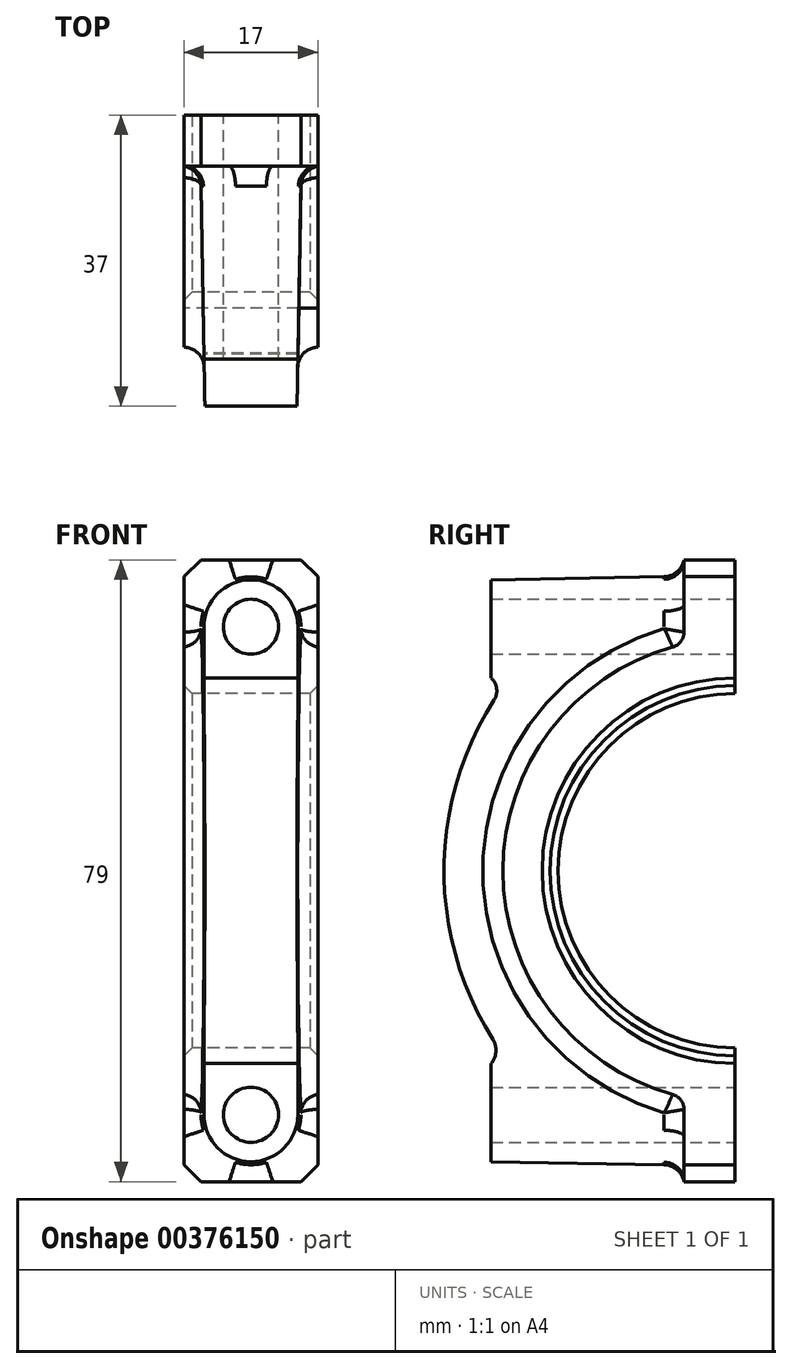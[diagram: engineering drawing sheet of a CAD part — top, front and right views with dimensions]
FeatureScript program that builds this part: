
annotation { "Feature Type Name" : "Feature", "Feature Type Description" : "" }
export const myFeature = defineFeature(function(context is Context, id is Id, definition is map)
    precondition{}
    {
        {
            var Q0;
            Q0=qCreatedBy(makeId("Top.planeOp"),FACE);
            var sketch = newSketch(context, id + "F0", { "sketchPlane" : qUnion([Q0])});
            skCircle(sketch, "E0", {"center": v(0, 31) * mm, "radius": 3.5 * mm});
            skCircle(sketch, "E1", {"center": v(0, 31) * mm, "radius": 6.5 * mm});
            skLineSegment(sketch, "E2", {"start": v(-13.97, 0) * mm, "end": v(15.82, 0) * mm, "construction": true});
            skLineSegment(sketch, "E3", {"start": v(-6.5, 31) * mm, "end": v(-6.5, 0) * mm});
            skLineSegment(sketch, "E4", {"start": v(-6.5, 0) * mm, "end": v(6.5, 0) * mm});
            skLineSegment(sketch, "E5", {"start": v(6.5, 0) * mm, "end": v(6.5, 31) * mm});
            skLineSegment(sketch, "E6", {"start": v(-6.35, 39.5) * mm, "end": v(6.35, 39.5) * mm});
            skLineSegment(sketch, "E7", {"start": v(6.35, 39.5) * mm, "end": v(8.5, 37.35) * mm});
            skLineSegment(sketch, "E8", {"start": v(8.5, 37.35) * mm, "end": v(8.5, 0) * mm});
            skLineSegment(sketch, "E9", {"start": v(8.5, 0) * mm, "end": v(-8.5, 0) * mm});
            skLineSegment(sketch, "E10", {"start": v(-8.5, 0) * mm, "end": v(-8.5, 37.35) * mm});
            skLineSegment(sketch, "E11", {"start": v(-8.5, 37.35) * mm, "end": v(-6.35, 39.5) * mm});
            skLineSegment(sketch, "E12", {"start": v(-6.5, 0) * mm, "end": v(-6.5, -31) * mm});
            skLineSegment(sketch, "E13", {"start": v(6.5, 0) * mm, "end": v(6.5, -31) * mm});
            skCircle(sketch, "E14", {"center": v(0, -31) * mm, "radius": 6.5 * mm});
            skCircle(sketch, "E15", {"center": v(0, -31) * mm, "radius": 3.5 * mm});
            skLineSegment(sketch, "E16", {"start": v(-8.5, 0) * mm, "end": v(-8.5, -37.35) * mm});
            skLineSegment(sketch, "E17", {"start": v(-8.5, -37.35) * mm, "end": v(-6.35, -39.5) * mm});
            skLineSegment(sketch, "E18", {"start": v(-6.35, -39.5) * mm, "end": v(6.35, -39.5) * mm});
            skLineSegment(sketch, "E19", {"start": v(6.35, -39.5) * mm, "end": v(8.5, -37.35) * mm});
            skLineSegment(sketch, "E20", {"start": v(8.5, -37.35) * mm, "end": v(8.5, 0) * mm});
            skSolve(sketch);
        }
        {
            var Q0;
            {var subQ1=sQuery(id+"F0.wireOp",EDGE,"E3");Q0=makeQuery(id+"F0.imprint","IMPRINT",FACE,{"disambiguationData":[TD([[makeQuery(id+"F0.imprint","IMPRINT",EDGE,{"derivedFrom":subQ1}),-1.0]])]});}
            var Q1;
            {var subQ0=sQuery(id+"F0.wireOp",EDGE,"E3");Q1=makeQuery(id+"F0.imprint","IMPRINT",FACE,{"disambiguationData":[TD([[makeQuery(id+"F0.imprint","IMPRINT",EDGE,{"derivedFrom":subQ0}),1.0]])]});}
            var Q2;
            Q2=makeQuery(id+"F0.imprint","IMPRINT",FACE,{"disambiguationData":[TD([[makeQuery(id+"F0.imprint","IMPRINT",EDGE,{"derivedFrom":sQuery(id+"F0.wireOp",EDGE,"E0")}),-1.0]])]});
            var Q3;
            Q3=makeQuery(id+"F0.imprint","IMPRINT",FACE,{"disambiguationData":[TD([[makeQuery(id+"F0.imprint","IMPRINT",EDGE,{"derivedFrom":sQuery(id+"F0.wireOp",EDGE,"E0")}),1.0]])]});
            var Q4;
            {var subQ1=sQuery(id+"F0.wireOp",EDGE,"E12");Q4=makeQuery(id+"F0.imprint","IMPRINT",FACE,{"disambiguationData":[TD([[makeQuery(id+"F0.imprint","IMPRINT",EDGE,{"derivedFrom":subQ1}),-1.0]])]});}
            var Q5;
            Q5=makeQuery(id+"F0.imprint","IMPRINT",FACE,{"disambiguationData":[TD([[makeQuery(id+"F0.imprint","IMPRINT",EDGE,{"derivedFrom":sQuery(id+"F0.wireOp",EDGE,"E15")}),-1.0]])]});
            var Q6;
            Q6=makeQuery(id+"F0.imprint","IMPRINT",FACE,{"disambiguationData":[TD([[makeQuery(id+"F0.imprint","IMPRINT",EDGE,{"derivedFrom":sQuery(id+"F0.wireOp",EDGE,"E15")}),1.0]])]});
            var Q7;
            {var subQ0=sQuery(id+"F0.wireOp",EDGE,"E12");Q7=makeQuery(id+"F0.imprint","IMPRINT",FACE,{"disambiguationData":[TD([[makeQuery(id+"F0.imprint","IMPRINT",EDGE,{"derivedFrom":subQ0}),1.0]])]});}
            extrude(context, id + "F1", {"entities" : qUnion([Q0, Q1, Q2, Q3, Q4, Q5, Q6, Q7]), "oppositeDirection" : true, "depth" : 6.5 * mm, "offsetDistance" : 25 * mm});
        }
        {
            var Q0;
            {var subQ0=sQuery(id+"F0.wireOp",EDGE,"E3");Q0=makeQuery(id+"F0.imprint","IMPRINT",FACE,{"disambiguationData":[TD([[makeQuery(id+"F0.imprint","IMPRINT",EDGE,{"derivedFrom":subQ0}),1.0]])]});}
            var Q1;
            Q1=makeQuery(id+"F0.imprint","IMPRINT",FACE,{"disambiguationData":[TD([[makeQuery(id+"F0.imprint","IMPRINT",EDGE,{"derivedFrom":sQuery(id+"F0.wireOp",EDGE,"E0")}),-1.0]])]});
            var Q2;
            Q2=makeQuery(id+"F0.imprint","IMPRINT",FACE,{"disambiguationData":[TD([[makeQuery(id+"F0.imprint","IMPRINT",EDGE,{"derivedFrom":sQuery(id+"F0.wireOp",EDGE,"E0")}),1.0]])]});
            var Q3;
            Q3=makeQuery(id+"F0.imprint","IMPRINT",FACE,{"disambiguationData":[TD([[makeQuery(id+"F0.imprint","IMPRINT",EDGE,{"derivedFrom":sQuery(id+"F0.wireOp",EDGE,"E15")}),-1.0]])]});
            var Q4;
            Q4=makeQuery(id+"F0.imprint","IMPRINT",FACE,{"disambiguationData":[TD([[makeQuery(id+"F0.imprint","IMPRINT",EDGE,{"derivedFrom":sQuery(id+"F0.wireOp",EDGE,"E15")}),1.0]])]});
            var Q5;
            {var subQ0=sQuery(id+"F0.wireOp",EDGE,"E12");Q5=makeQuery(id+"F0.imprint","IMPRINT",FACE,{"disambiguationData":[TD([[makeQuery(id+"F0.imprint","IMPRINT",EDGE,{"derivedFrom":subQ0}),1.0]])]});}
            extrude(context, id + "F2", {"entities" : qUnion([Q0, Q1, Q2, Q3, Q4, Q5]), "operationType" : NewBodyOperationType.ADD, "oppositeDirection" : true, "depth" : 40 * mm, "offsetDistance" : 25 * mm, "hasDraft" : true, "draftAngle" : 1 * degree, "draftPullDirection" : true});
        }
        {
            var Q0;
            Q0=qCreatedBy(makeId("Right.planeOp"),FACE);
            var sketch = newSketch(context, id + "F3", { "sketchPlane" : qUnion([Q0])});
            skArc(sketch, "E21", {"start": v(-22.5, 0) * mm, "mid": v(0, -22.5) * mm, "end": v(22.5, 0) * mm});
            skArc(sketch, "E22", {"start": v(-24.5, 0) * mm, "mid": v(0, -24.5) * mm, "end": v(24.5, 0) * mm});
            skArc(sketch, "E23", {"start": v(-29.5, 0) * mm, "mid": v(0, -29.5) * mm, "end": v(29.5, 0) * mm});
            skLineSegment(sketch, "E24", {"start": v(-29.5, 0) * mm, "end": v(29.5, 0) * mm});
            skArc(sketch, "E25", {"start": v(-21.67, -30.62) * mm, "mid": v(-0.15, -37) * mm, "end": v(21.42, -30.78) * mm});
            skLineSegment(sketch, "E26", {"start": v(0, 5.53) * mm, "end": v(0, -32.05) * mm, "construction": true});
            skLineSegment(sketch, "E27", {"start": v(-8.92, -37) * mm, "end": v(11.8, -37) * mm, "construction": true});
            skArc(sketch, "E28", {"start": v(-21.67, -30.62) * mm, "mid": v(-23.16, -30.29) * mm, "end": v(-24.5, -31) * mm});
            skLineSegment(sketch, "E29", {"start": v(-24.5, -31) * mm, "end": v(-45, -31) * mm});
            skLineSegment(sketch, "E30", {"start": v(-45, -31) * mm, "end": v(-45, -50) * mm});
            skLineSegment(sketch, "E31", {"start": v(-45, -50) * mm, "end": v(45, -50) * mm});
            skLineSegment(sketch, "E32", {"start": v(45, -50) * mm, "end": v(45, -31) * mm});
            skLineSegment(sketch, "E33", {"start": v(-24.5, 0) * mm, "end": v(-24.5, -60.37) * mm, "construction": true});
            skLineSegment(sketch, "E34", {"start": v(45, -31) * mm, "end": v(24.5, -31) * mm});
            skArc(sketch, "E35", {"start": v(24.5, -31) * mm, "mid": v(23, -30.38) * mm, "end": v(21.42, -30.78) * mm});
            skPoint(sketch, "E36", {"position": v(0, -29.5) * mm});
            skLineSegment(sketch, "E37", {"start": v(24.5, 0) * mm, "end": v(24.5, -59.56) * mm, "construction": true});
            skSolve(sketch);
        }
        {
            var Q0;
            {var subQ0=sQuery(id+"F3.wireOp",EDGE,"E22");Q0=makeQuery(id+"F3.imprint","IMPRINT",FACE,{"disambiguationData":[TD([[makeQuery(id+"F3.imprint","IMPRINT",EDGE,{"derivedFrom":subQ0}),-1.0]])]});}
            extrude(context, id + "F4", {"entities" : qUnion([Q0]), "operationType" : NewBodyOperationType.ADD, "endBound" : BoundingType.SYMMETRIC, "depth" : 17 * mm, "offsetDistance" : 25 * mm});
        }
        {
            var Q0;
            Q0=makeQuery(id+"F3.imprint","IMPRINT",FACE,{"disambiguationData":[TD([[makeQuery(id+"F3.imprint","IMPRINT",EDGE,{"derivedFrom":sQuery(id+"F3.wireOp",EDGE,"E21")}),-1.0]])]});
            var Q1;
            Q1=makeQuery(id+"F3.imprint","IMPRINT",FACE,{"disambiguationData":[TD([[makeQuery(id+"F3.imprint","IMPRINT",EDGE,{"derivedFrom":sQuery(id+"F3.wireOp",EDGE,"E21")}),1.0]])]});
            extrude(context, id + "F5", {"entities" : qUnion([Q0, Q1]), "operationType" : NewBodyOperationType.REMOVE, "endBound" : BoundingType.SYMMETRIC, "depth" : 100 * mm, "offsetDistance" : 25 * mm});
        }
        {
            var Q0;
            Q0=makeQuery(id+"F4.boolean.opBoolean","INTERSECT",EDGE,{"derivedFrom":[makeQuery(id+"F2.opExtrude","SWEPT_FACE",FACE,{"disambiguationData":[OSD([sQuery(id+"F0.wireOp",EDGE,"E5"),sQuery(id+"F0.wireOp",EDGE,"E13")])]}),makeQuery(id+"F4.opExtrude","SWEPT_FACE",FACE,{"disambiguationData":[OSD([sQuery(id+"F3.wireOp",EDGE,"E23")])]})]});
            var Q1;
            {var subQ0=makeQuery(id+"F1.opExtrude","CAP_FACE",FACE,{"disambiguationData":[OSD([sQuery(id+"F0.wireOp",EDGE,"E6"),sQuery(id+"F0.wireOp",EDGE,"E7"),sQuery(id+"F0.wireOp",EDGE,"E8"),sQuery(id+"F0.wireOp",EDGE,"E10"),sQuery(id+"F0.wireOp",EDGE,"E11"),sQuery(id+"F0.wireOp",EDGE,"E16"),sQuery(id+"F0.wireOp",EDGE,"E17"),sQuery(id+"F0.wireOp",EDGE,"E18"),sQuery(id+"F0.wireOp",EDGE,"E19"),sQuery(id+"F0.wireOp",EDGE,"E20")])],"isStart":false});var subQ1=makeQuery(id+"F2.opExtrude","SWEPT_FACE",FACE,{"disambiguationData":[OSD([sQuery(id+"F0.wireOp",EDGE,"E5"),sQuery(id+"F0.wireOp",EDGE,"E13")])]});Q1=makeQuery(id+"F4.boolean.opBoolean","SPLIT",EDGE,{"disambiguationData":[TD([makeQuery(id+"F2.opExtrude","SWEPT_FACE",FACE,{"disambiguationData":[OSD([sQuery(id+"F0.wireOp",EDGE,"E14")])]})])],"derivedFrom":makeQuery(id+"F2.boolean.opBoolean","INTERSECT",EDGE,{"derivedFrom":[subQ0,subQ1]})});}
            var Q2;
            Q2=makeQuery(id+"F2.boolean.opBoolean","INTERSECT",EDGE,{"derivedFrom":[makeQuery(id+"F1.opExtrude","CAP_FACE",FACE,{"disambiguationData":[OSD([sQuery(id+"F0.wireOp",EDGE,"E6"),sQuery(id+"F0.wireOp",EDGE,"E7"),sQuery(id+"F0.wireOp",EDGE,"E8"),sQuery(id+"F0.wireOp",EDGE,"E10"),sQuery(id+"F0.wireOp",EDGE,"E11"),sQuery(id+"F0.wireOp",EDGE,"E16"),sQuery(id+"F0.wireOp",EDGE,"E17"),sQuery(id+"F0.wireOp",EDGE,"E18"),sQuery(id+"F0.wireOp",EDGE,"E19"),sQuery(id+"F0.wireOp",EDGE,"E20")])],"isStart":false}),makeQuery(id+"F2.opExtrude","SWEPT_FACE",FACE,{"disambiguationData":[OSD([sQuery(id+"F0.wireOp",EDGE,"E14")])]})]});
            var Q3;
            {var subQ0=makeQuery(id+"F1.opExtrude","CAP_FACE",FACE,{"disambiguationData":[OSD([sQuery(id+"F0.wireOp",EDGE,"E6"),sQuery(id+"F0.wireOp",EDGE,"E7"),sQuery(id+"F0.wireOp",EDGE,"E8"),sQuery(id+"F0.wireOp",EDGE,"E10"),sQuery(id+"F0.wireOp",EDGE,"E11"),sQuery(id+"F0.wireOp",EDGE,"E16"),sQuery(id+"F0.wireOp",EDGE,"E17"),sQuery(id+"F0.wireOp",EDGE,"E18"),sQuery(id+"F0.wireOp",EDGE,"E19"),sQuery(id+"F0.wireOp",EDGE,"E20")])],"isStart":false});var subQ1=makeQuery(id+"F2.opExtrude","SWEPT_FACE",FACE,{"disambiguationData":[OSD([sQuery(id+"F0.wireOp",EDGE,"E5"),sQuery(id+"F0.wireOp",EDGE,"E13")])]});Q3=makeQuery(id+"F4.boolean.opBoolean","SPLIT",EDGE,{"disambiguationData":[TD([makeQuery(id+"F2.opExtrude","SWEPT_FACE",FACE,{"disambiguationData":[OSD([sQuery(id+"F0.wireOp",EDGE,"E1")])]})])],"derivedFrom":makeQuery(id+"F2.boolean.opBoolean","INTERSECT",EDGE,{"derivedFrom":[subQ0,subQ1]})});}
            var Q4;
            Q4=makeQuery(id+"F2.boolean.opBoolean","INTERSECT",EDGE,{"derivedFrom":[makeQuery(id+"F1.opExtrude","CAP_FACE",FACE,{"disambiguationData":[OSD([sQuery(id+"F0.wireOp",EDGE,"E6"),sQuery(id+"F0.wireOp",EDGE,"E7"),sQuery(id+"F0.wireOp",EDGE,"E8"),sQuery(id+"F0.wireOp",EDGE,"E10"),sQuery(id+"F0.wireOp",EDGE,"E11"),sQuery(id+"F0.wireOp",EDGE,"E16"),sQuery(id+"F0.wireOp",EDGE,"E17"),sQuery(id+"F0.wireOp",EDGE,"E18"),sQuery(id+"F0.wireOp",EDGE,"E19"),sQuery(id+"F0.wireOp",EDGE,"E20")])],"isStart":false}),makeQuery(id+"F2.opExtrude","SWEPT_FACE",FACE,{"disambiguationData":[OSD([sQuery(id+"F0.wireOp",EDGE,"E1")])]})]});
            var Q5;
            {var subQ0=makeQuery(id+"F1.opExtrude","CAP_FACE",FACE,{"disambiguationData":[OSD([sQuery(id+"F0.wireOp",EDGE,"E6"),sQuery(id+"F0.wireOp",EDGE,"E7"),sQuery(id+"F0.wireOp",EDGE,"E8"),sQuery(id+"F0.wireOp",EDGE,"E10"),sQuery(id+"F0.wireOp",EDGE,"E11"),sQuery(id+"F0.wireOp",EDGE,"E16"),sQuery(id+"F0.wireOp",EDGE,"E17"),sQuery(id+"F0.wireOp",EDGE,"E18"),sQuery(id+"F0.wireOp",EDGE,"E19"),sQuery(id+"F0.wireOp",EDGE,"E20")])],"isStart":false});var subQ1=makeQuery(id+"F2.opExtrude","SWEPT_FACE",FACE,{"disambiguationData":[OSD([sQuery(id+"F0.wireOp",EDGE,"E3"),sQuery(id+"F0.wireOp",EDGE,"E12")])]});Q5=makeQuery(id+"F4.boolean.opBoolean","SPLIT",EDGE,{"disambiguationData":[TD([makeQuery(id+"F2.opExtrude","SWEPT_FACE",FACE,{"disambiguationData":[OSD([sQuery(id+"F0.wireOp",EDGE,"E1")])]})])],"derivedFrom":makeQuery(id+"F2.boolean.opBoolean","INTERSECT",EDGE,{"derivedFrom":[subQ0,subQ1]})});}
            var Q6;
            Q6=makeQuery(id+"F4.boolean.opBoolean","INTERSECT",EDGE,{"derivedFrom":[makeQuery(id+"F2.opExtrude","SWEPT_FACE",FACE,{"disambiguationData":[OSD([sQuery(id+"F0.wireOp",EDGE,"E3"),sQuery(id+"F0.wireOp",EDGE,"E12")])]}),makeQuery(id+"F4.opExtrude","SWEPT_FACE",FACE,{"disambiguationData":[OSD([sQuery(id+"F3.wireOp",EDGE,"E23")])]})]});
            var Q7;
            {var subQ0=makeQuery(id+"F1.opExtrude","CAP_FACE",FACE,{"disambiguationData":[OSD([sQuery(id+"F0.wireOp",EDGE,"E6"),sQuery(id+"F0.wireOp",EDGE,"E7"),sQuery(id+"F0.wireOp",EDGE,"E8"),sQuery(id+"F0.wireOp",EDGE,"E10"),sQuery(id+"F0.wireOp",EDGE,"E11"),sQuery(id+"F0.wireOp",EDGE,"E16"),sQuery(id+"F0.wireOp",EDGE,"E17"),sQuery(id+"F0.wireOp",EDGE,"E18"),sQuery(id+"F0.wireOp",EDGE,"E19"),sQuery(id+"F0.wireOp",EDGE,"E20")])],"isStart":false});var subQ1=makeQuery(id+"F2.opExtrude","SWEPT_FACE",FACE,{"disambiguationData":[OSD([sQuery(id+"F0.wireOp",EDGE,"E3"),sQuery(id+"F0.wireOp",EDGE,"E12")])]});Q7=makeQuery(id+"F4.boolean.opBoolean","SPLIT",EDGE,{"disambiguationData":[TD([makeQuery(id+"F2.opExtrude","SWEPT_FACE",FACE,{"disambiguationData":[OSD([sQuery(id+"F0.wireOp",EDGE,"E14")])]})])],"derivedFrom":makeQuery(id+"F2.boolean.opBoolean","INTERSECT",EDGE,{"derivedFrom":[subQ0,subQ1]})});}
            fillet(context, id + "F6", {"entities" : qUnion([Q0, Q1, Q2, Q3, Q4, Q5, Q6, Q7]), "radius" : 2.6 * mm, "tangentPropagation" : true, "allowEdgeOverflow" : false});
        }
        {
            var Q0;
            Q0=makeQuery(id+"F0.imprint","IMPRINT",FACE,{"disambiguationData":[TD([[makeQuery(id+"F0.imprint","IMPRINT",EDGE,{"derivedFrom":sQuery(id+"F0.wireOp",EDGE,"E15")}),1.0]])]});
            var Q1;
            Q1=makeQuery(id+"F0.imprint","IMPRINT",FACE,{"disambiguationData":[TD([[makeQuery(id+"F0.imprint","IMPRINT",EDGE,{"derivedFrom":sQuery(id+"F0.wireOp",EDGE,"E0")}),1.0]])]});
            extrude(context, id + "F7", {"entities" : qUnion([Q0, Q1]), "operationType" : NewBodyOperationType.REMOVE, "endBound" : BoundingType.THROUGH_ALL, "oppositeDirection" : true, "depth" : 25 * mm, "offsetDistance" : 25 * mm});
        }
        {
            var Q0;
            Q0=makeQuery(id+"F3.imprint","IMPRINT",FACE,{"disambiguationData":[TD([[makeQuery(id+"F3.imprint","IMPRINT",EDGE,{"derivedFrom":sQuery(id+"F3.wireOp",EDGE,"E25")}),-1.0]])]});
            extrude(context, id + "F8", {"entities" : qUnion([Q0]), "operationType" : NewBodyOperationType.REMOVE, "endBound" : BoundingType.SYMMETRIC, "depth" : 100 * mm, "offsetDistance" : 25 * mm});
        }
        {
            var Q0;
            {var subQ0=makeQuery(id+"F4.opExtrude","SWEPT_FACE",FACE,{"disambiguationData":[OSD([sQuery(id+"F3.wireOp",EDGE,"E23")])]});var subQ1=makeQuery(id+"F2.opExtrude","SWEPT_FACE",FACE,{"disambiguationData":[OSD([sQuery(id+"F0.wireOp",EDGE,"E5"),sQuery(id+"F0.wireOp",EDGE,"E13")])]});var subQ2=subQ1;var subQ3=makeQuery(id+"F1.opExtrude","CAP_FACE",FACE,{"disambiguationData":[OSD([sQuery(id+"F0.wireOp",EDGE,"E6"),sQuery(id+"F0.wireOp",EDGE,"E7"),sQuery(id+"F0.wireOp",EDGE,"E8"),sQuery(id+"F0.wireOp",EDGE,"E10"),sQuery(id+"F0.wireOp",EDGE,"E11"),sQuery(id+"F0.wireOp",EDGE,"E16"),sQuery(id+"F0.wireOp",EDGE,"E17"),sQuery(id+"F0.wireOp",EDGE,"E18"),sQuery(id+"F0.wireOp",EDGE,"E19"),sQuery(id+"F0.wireOp",EDGE,"E20")])],"isStart":false});Q0=makeQuery(id+"F6.opFillet","BLEND_EDGE",EDGE,{"blendedFrom":[makeQuery(id+"F4.boolean.opBoolean","SPLIT",EDGE,{"disambiguationData":[TD([makeQuery(id+"F2.opExtrude","SWEPT_FACE",FACE,{"disambiguationData":[OSD([sQuery(id+"F0.wireOp",EDGE,"E1")])]})])],"derivedFrom":makeQuery(id+"F2.boolean.opBoolean","INTERSECT",EDGE,{"derivedFrom":[subQ3,subQ2]})}),makeQuery(id+"F4.boolean.opBoolean","INTERSECT",EDGE,{"derivedFrom":[subQ2,subQ0]})],"blendedInto":[]});}
            var Q1;
            {var subQ0=makeQuery(id+"F4.opExtrude","SWEPT_FACE",FACE,{"disambiguationData":[OSD([sQuery(id+"F3.wireOp",EDGE,"E23")])]});var subQ1=makeQuery(id+"F2.opExtrude","SWEPT_FACE",FACE,{"disambiguationData":[OSD([sQuery(id+"F0.wireOp",EDGE,"E5"),sQuery(id+"F0.wireOp",EDGE,"E13")])]});var subQ2=subQ1;var subQ3=makeQuery(id+"F1.opExtrude","CAP_FACE",FACE,{"disambiguationData":[OSD([sQuery(id+"F0.wireOp",EDGE,"E6"),sQuery(id+"F0.wireOp",EDGE,"E7"),sQuery(id+"F0.wireOp",EDGE,"E8"),sQuery(id+"F0.wireOp",EDGE,"E10"),sQuery(id+"F0.wireOp",EDGE,"E11"),sQuery(id+"F0.wireOp",EDGE,"E16"),sQuery(id+"F0.wireOp",EDGE,"E17"),sQuery(id+"F0.wireOp",EDGE,"E18"),sQuery(id+"F0.wireOp",EDGE,"E19"),sQuery(id+"F0.wireOp",EDGE,"E20")])],"isStart":false});Q1=makeQuery(id+"F6.opFillet","BLEND_EDGE",EDGE,{"blendedFrom":[makeQuery(id+"F4.boolean.opBoolean","SPLIT",EDGE,{"disambiguationData":[TD([makeQuery(id+"F2.opExtrude","SWEPT_FACE",FACE,{"disambiguationData":[OSD([sQuery(id+"F0.wireOp",EDGE,"E14")])]})])],"derivedFrom":makeQuery(id+"F2.boolean.opBoolean","INTERSECT",EDGE,{"derivedFrom":[subQ3,subQ2]})}),makeQuery(id+"F4.boolean.opBoolean","INTERSECT",EDGE,{"derivedFrom":[subQ2,subQ0]})],"blendedInto":[]});}
            var Q2;
            {var subQ0=makeQuery(id+"F4.opExtrude","SWEPT_FACE",FACE,{"disambiguationData":[OSD([sQuery(id+"F3.wireOp",EDGE,"E23")])]});var subQ1=makeQuery(id+"F2.opExtrude","SWEPT_FACE",FACE,{"disambiguationData":[OSD([sQuery(id+"F0.wireOp",EDGE,"E3"),sQuery(id+"F0.wireOp",EDGE,"E12")])]});var subQ2=subQ1;var subQ3=makeQuery(id+"F1.opExtrude","CAP_FACE",FACE,{"disambiguationData":[OSD([sQuery(id+"F0.wireOp",EDGE,"E6"),sQuery(id+"F0.wireOp",EDGE,"E7"),sQuery(id+"F0.wireOp",EDGE,"E8"),sQuery(id+"F0.wireOp",EDGE,"E10"),sQuery(id+"F0.wireOp",EDGE,"E11"),sQuery(id+"F0.wireOp",EDGE,"E16"),sQuery(id+"F0.wireOp",EDGE,"E17"),sQuery(id+"F0.wireOp",EDGE,"E18"),sQuery(id+"F0.wireOp",EDGE,"E19"),sQuery(id+"F0.wireOp",EDGE,"E20")])],"isStart":false});Q2=makeQuery(id+"F6.opFillet","BLEND_EDGE",EDGE,{"blendedFrom":[makeQuery(id+"F4.boolean.opBoolean","SPLIT",EDGE,{"disambiguationData":[TD([makeQuery(id+"F2.opExtrude","SWEPT_FACE",FACE,{"disambiguationData":[OSD([sQuery(id+"F0.wireOp",EDGE,"E14")])]})])],"derivedFrom":makeQuery(id+"F2.boolean.opBoolean","INTERSECT",EDGE,{"derivedFrom":[subQ3,subQ2]})}),makeQuery(id+"F4.boolean.opBoolean","INTERSECT",EDGE,{"derivedFrom":[subQ2,subQ0]})],"blendedInto":[]});}
            var Q3;
            {var subQ0=makeQuery(id+"F4.opExtrude","SWEPT_FACE",FACE,{"disambiguationData":[OSD([sQuery(id+"F3.wireOp",EDGE,"E23")])]});var subQ1=makeQuery(id+"F2.opExtrude","SWEPT_FACE",FACE,{"disambiguationData":[OSD([sQuery(id+"F0.wireOp",EDGE,"E3"),sQuery(id+"F0.wireOp",EDGE,"E12")])]});var subQ2=subQ1;var subQ3=makeQuery(id+"F1.opExtrude","CAP_FACE",FACE,{"disambiguationData":[OSD([sQuery(id+"F0.wireOp",EDGE,"E6"),sQuery(id+"F0.wireOp",EDGE,"E7"),sQuery(id+"F0.wireOp",EDGE,"E8"),sQuery(id+"F0.wireOp",EDGE,"E10"),sQuery(id+"F0.wireOp",EDGE,"E11"),sQuery(id+"F0.wireOp",EDGE,"E16"),sQuery(id+"F0.wireOp",EDGE,"E17"),sQuery(id+"F0.wireOp",EDGE,"E18"),sQuery(id+"F0.wireOp",EDGE,"E19"),sQuery(id+"F0.wireOp",EDGE,"E20")])],"isStart":false});Q3=makeQuery(id+"F6.opFillet","BLEND_EDGE",EDGE,{"blendedFrom":[makeQuery(id+"F4.boolean.opBoolean","SPLIT",EDGE,{"disambiguationData":[TD([makeQuery(id+"F2.opExtrude","SWEPT_FACE",FACE,{"disambiguationData":[OSD([sQuery(id+"F0.wireOp",EDGE,"E1")])]})])],"derivedFrom":makeQuery(id+"F2.boolean.opBoolean","INTERSECT",EDGE,{"derivedFrom":[subQ3,subQ2]})}),makeQuery(id+"F4.boolean.opBoolean","INTERSECT",EDGE,{"derivedFrom":[subQ2,subQ0]})],"blendedInto":[]});}
            fillet(context, id + "F9", {"entities" : qUnion([Q0, Q1, Q2, Q3]), "radius" : 2 * mm, "tangentPropagation" : true, "allowEdgeOverflow" : false});
        }
        {
            var Q0;
            {var subQ0=sQuery(id+"F3.wireOp",EDGE,"E21");Q0=makeQuery(id+"F3.imprint","IMPRINT",FACE,{"disambiguationData":[TD([[makeQuery(id+"F3.imprint","IMPRINT",EDGE,{"derivedFrom":subQ0}),-1.0]])]});}
            extrude(context, id + "F10", {"entities" : qUnion([Q0]), "endBound" : BoundingType.SYMMETRIC, "depth" : 17 * mm, "offsetDistance" : 25 * mm});
        }
        {
            var Q0;
            Q0=makeQuery(id+"F1.opExtrude","SWEPT_BODY",BODY,{"disambiguationData":[OSD([sQuery(id+"F0.wireOp",EDGE,"E6"),sQuery(id+"F0.wireOp",EDGE,"E7"),sQuery(id+"F0.wireOp",EDGE,"E8"),sQuery(id+"F0.wireOp",EDGE,"E10"),sQuery(id+"F0.wireOp",EDGE,"E11"),sQuery(id+"F0.wireOp",EDGE,"E16"),sQuery(id+"F0.wireOp",EDGE,"E17"),sQuery(id+"F0.wireOp",EDGE,"E18"),sQuery(id+"F0.wireOp",EDGE,"E19"),sQuery(id+"F0.wireOp",EDGE,"E20")])]});
            var Q1;
            Q1=makeQuery(id+"F10.opExtrude","SWEPT_BODY",BODY,{"disambiguationData":[OSD([sQuery(id+"F3.wireOp",EDGE,"E21"),sQuery(id+"F3.wireOp",EDGE,"E22"),sQuery(id+"F3.wireOp",EDGE,"E24")])]});
            var Q2;
            Q2=sQuery(id+"F0.wireOp",EDGE,"E2");
            transform(context, id + "F11", {"entities" : qUnion([Q0, Q1]), "transformType" : TransformType.ROTATION, "transformAxis" : qUnion([Q2]), "angle" : 90 * degree, "oppositeDirection" : true, "makeCopy" : false});
        }
        {
            var Q0;
            Q0=makeQuery(id+"F10.opExtrude","CAP_EDGE",EDGE,{"disambiguationData":[OSD([sQuery(id+"F3.wireOp",EDGE,"E21")])],"isStart":true});
            var Q1;
            Q1=makeQuery(id+"F10.opExtrude","CAP_EDGE",EDGE,{"disambiguationData":[OSD([sQuery(id+"F3.wireOp",EDGE,"E21")])],"isStart":false});
            chamfer(context, id + "F12", {"entities" : qUnion([Q0, Q1]), "width" : 1 * mm, "tangentPropagation" : true});
        }
    });
